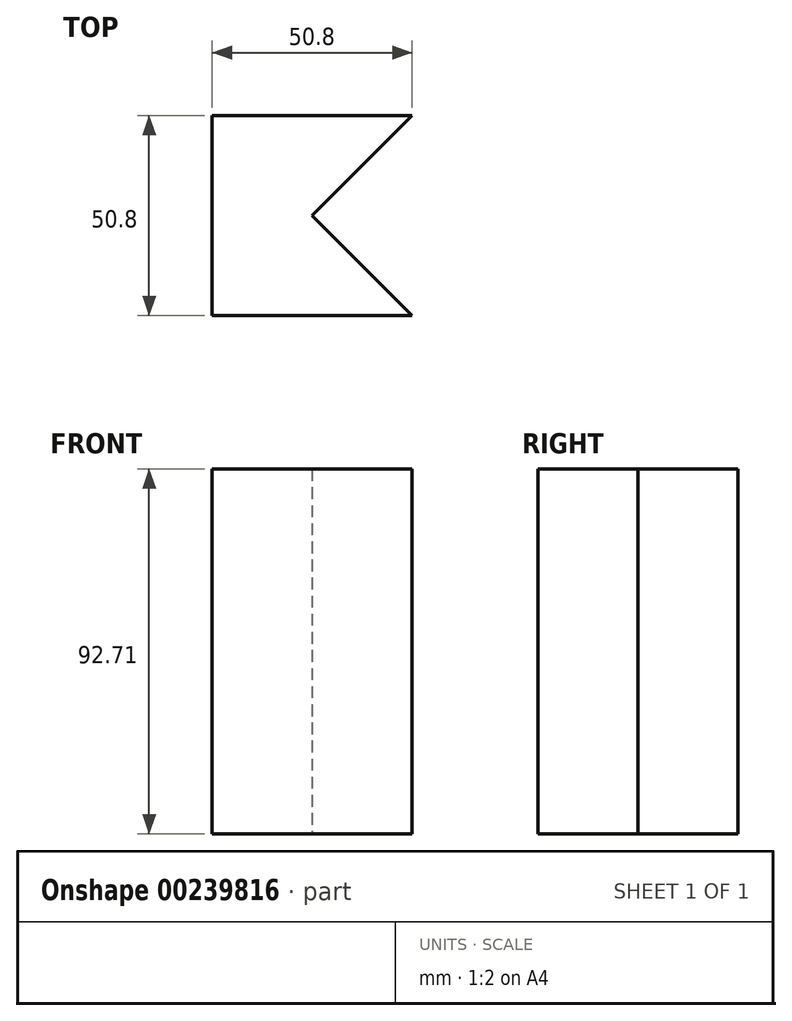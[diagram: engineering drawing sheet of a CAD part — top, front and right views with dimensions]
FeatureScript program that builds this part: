
annotation { "Feature Type Name" : "Feature", "Feature Type Description" : "" }
export const myFeature = defineFeature(function(context is Context, id is Id, definition is map)
    precondition{}
    {
        {
            var Q0;
            Q0=qCreatedBy(makeId("Top.planeOp"),FACE);
            var sketch = newSketch(context, id + "F0", { "sketchPlane" : qUnion([Q0])});
            skLineSegment(sketch, "E0", {"start": v(0, 0) * mm, "end": v(-50.8, 0) * mm});
            skLineSegment(sketch, "E1", {"start": v(-50.8, 0) * mm, "end": v(-50.8, -50.8) * mm});
            skLineSegment(sketch, "E2", {"start": v(-50.8, -50.8) * mm, "end": v(0, -50.8) * mm});
            skLineSegment(sketch, "E3", {"start": v(0, -50.8) * mm, "end": v(-25.4, -25.4) * mm});
            skLineSegment(sketch, "E4", {"start": v(-25.4, -25.4) * mm, "end": v(0, 0) * mm});
            skLineSegment(sketch, "E5", {"start": v(0, 0) * mm, "end": v(0, -50.8) * mm, "construction": true});
            skSolve(sketch);
        }
        {
            var Q0;
            Q0 = qSketchRegion(id + "F0", true);
            extrude(context, id + "F1", {"entities" : qUnion([Q0]), "depth" : 92.7 * mm});
        }
    });
